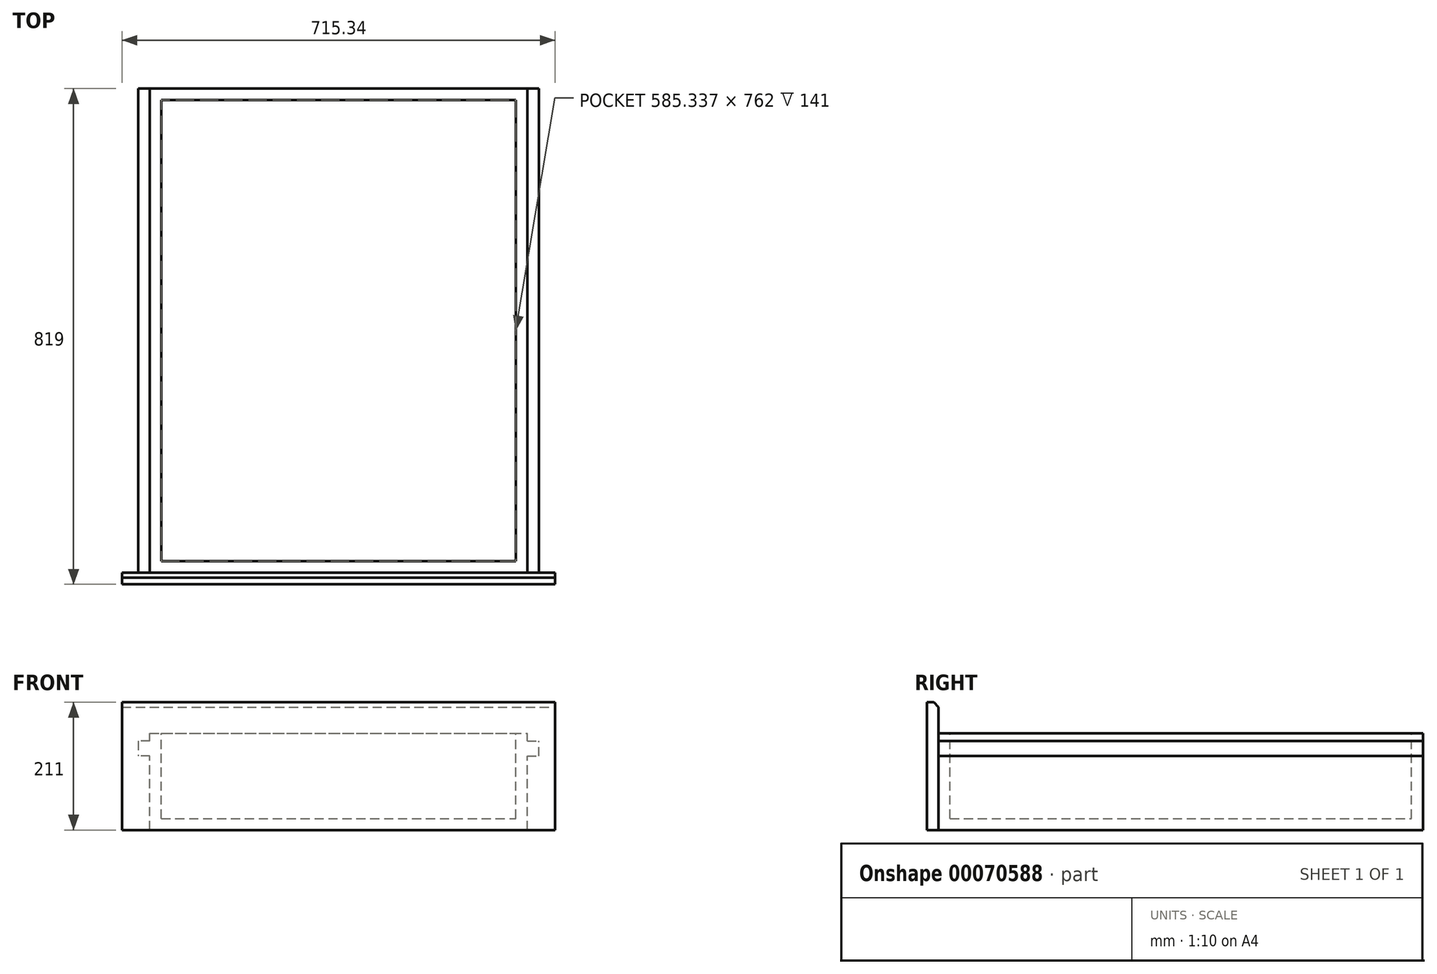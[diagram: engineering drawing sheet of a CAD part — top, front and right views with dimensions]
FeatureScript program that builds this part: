
annotation { "Feature Type Name" : "Feature", "Feature Type Description" : "" }
export const myFeature = defineFeature(function(context is Context, id is Id, definition is map)
    precondition{}
    {
        {
            var Q0;
            Q0=qCreatedBy(makeId("Front.planeOp"),FACE);
            var sketch = newSketch(context, id + "F0", { "sketchPlane" : qUnion([Q0])});
            skLineSegment(sketch, "E0.bottom", {"start": v(0, 0) * mm, "end": v(623.34, 0) * mm});
            skLineSegment(sketch, "E0.top", {"start": v(0, 160) * mm, "end": v(623.34, 160) * mm});
            skLineSegment(sketch, "E0.left", {"start": v(0, 0) * mm, "end": v(0, 160) * mm});
            skLineSegment(sketch, "E0.right", {"start": v(623.34, 0) * mm, "end": v(623.34, 160) * mm});
            skSolve(sketch);
        }
        {
            var Q0;
            Q0=qSketchRegion(id+"F0",true);
            extrude(context, id + "F1", {"entities" : qUnion([Q0]), "depth" : 800 * mm});
        }
        {
            var Q0;
            Q0=makeQuery(id+"F1.opExtrude","SWEPT_FACE",FACE,{"disambiguationData":[OSD([sQuery(id+"F0.wireOp",EDGE,"E0.top")])]});
            shell(context, id + "F2", {"entities" : qUnion([Q0]), "thickness" : 19 * mm});
        }
        {
            var Q0;
            Q0=makeQuery(id+"F1.opExtrude","CAP_FACE",FACE,{"disambiguationData":[OSD([sQuery(id+"F0.wireOp",EDGE,"E0.bottom"),sQuery(id+"F0.wireOp",EDGE,"E0.top"),sQuery(id+"F0.wireOp",EDGE,"E0.left"),sQuery(id+"F0.wireOp",EDGE,"E0.right")])],"isStart":false});
            var sketch = newSketch(context, id + "F3", { "sketchPlane" : qUnion([Q0])});
            skLineSegment(sketch, "E1.bottom", {"start": v(0, 147) * mm, "end": v(-19, 147) * mm});
            skLineSegment(sketch, "E1.top", {"start": v(0, 122) * mm, "end": v(-19, 122) * mm});
            skLineSegment(sketch, "E1.left", {"start": v(0, 147) * mm, "end": v(0, 122) * mm});
            skLineSegment(sketch, "E1.right", {"start": v(-19, 147) * mm, "end": v(-19, 122) * mm});
            skLineSegment(sketch, "E2.bottom", {"start": v(623.34, 122) * mm, "end": v(642.34, 122) * mm});
            skLineSegment(sketch, "E2.top", {"start": v(623.34, 147) * mm, "end": v(642.34, 147) * mm});
            skLineSegment(sketch, "E2.left", {"start": v(623.34, 122) * mm, "end": v(623.34, 147) * mm});
            skLineSegment(sketch, "E2.right", {"start": v(642.34, 122) * mm, "end": v(642.34, 147) * mm});
            skSolve(sketch);
        }
        {
            var Q0;
            Q0=qSketchRegion(id+"F3",true);
            extrude(context, id + "F4", {"entities" : qUnion([Q0]), "oppositeDirection" : true, "depth" : 800 * mm});
        }
        {
            var Q0;
            Q0=makeQuery(id+"F1.opExtrude","SWEPT_BODY",BODY,{"disambiguationData":[OSD([sQuery(id+"F0.wireOp",EDGE,"E0.bottom"),sQuery(id+"F0.wireOp",EDGE,"E0.top"),sQuery(id+"F0.wireOp",EDGE,"E0.left"),sQuery(id+"F0.wireOp",EDGE,"E0.right")])]});
            var Q1;
            Q1=makeQuery(id+"F4.opExtrude","SWEPT_BODY",BODY,{"disambiguationData":[OSD([sQuery(id+"F3.wireOp",EDGE,"E1.bottom"),sQuery(id+"F3.wireOp",EDGE,"E1.top"),sQuery(id+"F3.wireOp",EDGE,"E1.left"),sQuery(id+"F3.wireOp",EDGE,"E1.right")])]});
            var Q2;
            Q2=makeQuery(id+"F4.opExtrude","SWEPT_BODY",BODY,{"disambiguationData":[OSD([sQuery(id+"F3.wireOp",EDGE,"E2.bottom"),sQuery(id+"F3.wireOp",EDGE,"E2.top"),sQuery(id+"F3.wireOp",EDGE,"E2.left"),sQuery(id+"F3.wireOp",EDGE,"E2.right")])]});
            booleanBodies(context, id + "F5", {"operationType" : BooleanOperationType.UNION, "tools" : qUnion([Q0, Q1, Q2])});
        }
        {
            var Q0;
            Q0=makeQuery(id+"F5.opBoolean","MERGE",FACE,{"derivedFrom":[makeQuery(id+"F1.opExtrude","CAP_FACE",FACE,{"disambiguationData":[OSD([sQuery(id+"F0.wireOp",EDGE,"E0.bottom"),sQuery(id+"F0.wireOp",EDGE,"E0.top"),sQuery(id+"F0.wireOp",EDGE,"E0.left"),sQuery(id+"F0.wireOp",EDGE,"E0.right")])],"isStart":false}),makeQuery(id+"F4.opExtrude","CAP_FACE",FACE,{"disambiguationData":[OSD([sQuery(id+"F3.wireOp",EDGE,"E1.bottom"),sQuery(id+"F3.wireOp",EDGE,"E1.top"),sQuery(id+"F3.wireOp",EDGE,"E1.left"),sQuery(id+"F3.wireOp",EDGE,"E1.right")])],"isStart":true}),makeQuery(id+"F4.opExtrude","CAP_FACE",FACE,{"disambiguationData":[OSD([sQuery(id+"F3.wireOp",EDGE,"E2.bottom"),sQuery(id+"F3.wireOp",EDGE,"E2.top"),sQuery(id+"F3.wireOp",EDGE,"E2.left"),sQuery(id+"F3.wireOp",EDGE,"E2.right")])],"isStart":true})]});
            var sketch = newSketch(context, id + "F6", { "sketchPlane" : qUnion([Q0])});
            skLineSegment(sketch, "E3.bottom", {"start": v(-46, 0) * mm, "end": v(669.34, 0) * mm});
            skLineSegment(sketch, "E3.top", {"start": v(-46, 211) * mm, "end": v(669.34, 211) * mm});
            skLineSegment(sketch, "E3.left", {"start": v(-46, 0) * mm, "end": v(-46, 211) * mm});
            skLineSegment(sketch, "E3.right", {"start": v(669.34, 0) * mm, "end": v(669.34, 211) * mm});
            skSolve(sketch);
        }
        {
            var Q0;
            Q0=qSketchRegion(id+"F6",true);
            extrude(context, id + "F7", {"entities" : qUnion([Q0]), "operationType" : NewBodyOperationType.ADD, "depth" : 19 * mm});
        }
        {
            var Q0;
            Q0=makeQuery(id+"F7.opExtrude","CAP_FACE",FACE,{"disambiguationData":[OSD([sQuery(id+"F6.wireOp",EDGE,"E3.bottom"),sQuery(id+"F6.wireOp",EDGE,"E3.top"),sQuery(id+"F6.wireOp",EDGE,"E3.left"),sQuery(id+"F6.wireOp",EDGE,"E3.right")])],"isStart":false});
            var sketch = newSketch(context, id + "F8", { "sketchPlane" : qUnion([Q0])});
            skLineSegment(sketch, "E4.bottom", {"start": v(-46, 211) * mm, "end": v(114, 211) * mm});
            skLineSegment(sketch, "E4.top", {"start": v(-46, 171) * mm, "end": v(114, 171) * mm});
            skLineSegment(sketch, "E4.left", {"start": v(-46, 211) * mm, "end": v(-46, 171) * mm});
            skLineSegment(sketch, "E4.right", {"start": v(114, 211) * mm, "end": v(114, 171) * mm});
            skLineSegment(sketch, "E5.bottom", {"start": v(669.34, 211) * mm, "end": v(509.34, 211) * mm});
            skLineSegment(sketch, "E5.top", {"start": v(669.34, 171) * mm, "end": v(509.34, 171) * mm});
            skLineSegment(sketch, "E5.left", {"start": v(669.34, 211) * mm, "end": v(669.34, 171) * mm});
            skLineSegment(sketch, "E5.right", {"start": v(509.34, 211) * mm, "end": v(509.34, 171) * mm});
            skSolve(sketch);
        }
        {
            var Q0;
            Q0=makeQuery(id+"F7.opExtrude","CAP_EDGE",EDGE,{"disambiguationData":[OSD([sQuery(id+"F6.wireOp",EDGE,"E3.top")])],"isStart":true});
            chamfer(context, id + "F9", {"entities" : qUnion([Q0]), "width" : 8 * mm, "tangentPropagation" : true});
        }
    });
